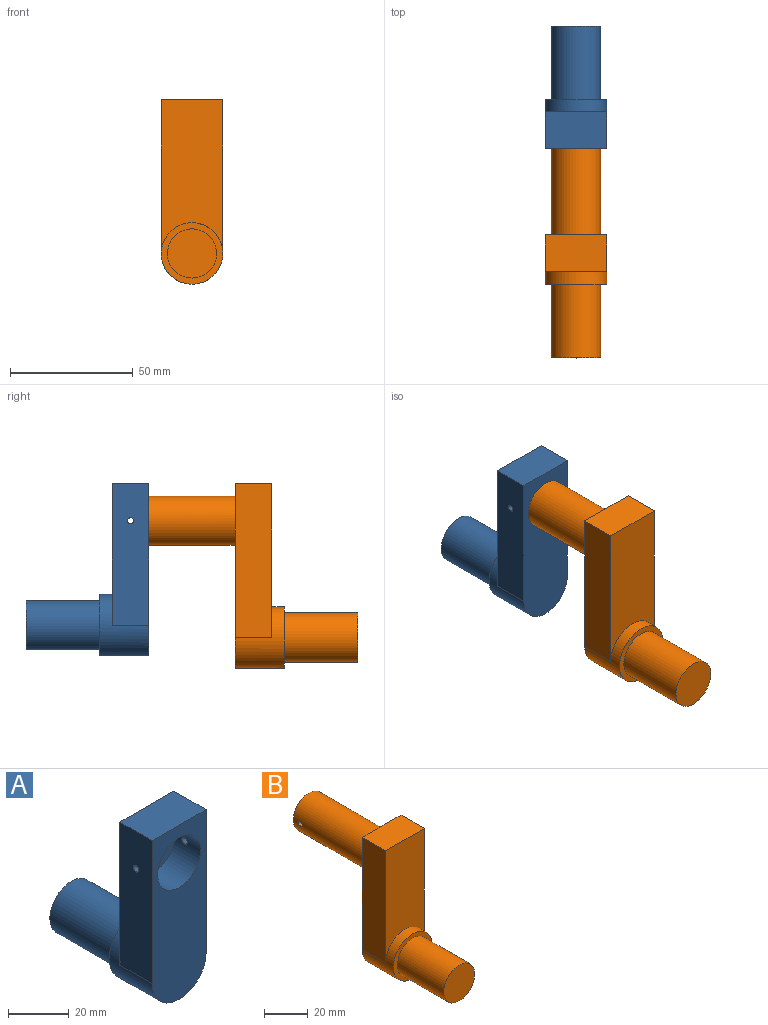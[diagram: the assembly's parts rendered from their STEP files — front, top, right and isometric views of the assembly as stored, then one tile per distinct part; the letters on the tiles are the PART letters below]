
ASSEMBLY  parts=2 mates=1
PART A: 13 faces, bbox 25x50x70 mm
  f0: plane 25x15mm, normal (0,0,1), area 375mm2, adj f1,f3,f4,f5
  f1: plane 57.5x15mm, normal (-1,0,0), area 857.6mm2, adj f0,f2,f4,f5,f12
  f2: cylinder r=12.5mm len=25mm, axis (0,1,0), area 981.7mm2, adj f1,f3,f4,f5,f6
  f3: plane 57.5x15mm, normal (1,0,0), area 857.6mm2, adj f0,f2,f4,f5,f11
  f4: plane 70x25mm, normal (0,-1,0), area 1368.8mm2, adj f0,f1,f2,f3,f9
  f5: plane 57.5x25mm, normal (0,1,0), area 1192.1mm2, adj f0,f1,f2,f3
  f6: plane 25x25mm, normal (0,1,0), area 176.7mm2, adj f2,f7
  f7: cylinder r=10mm len=30mm, axis (0,-1,0), area 1885mm2, adj f6,f8
  f8: plane 20x20mm, normal (0,1,0), area 314.2mm2, adj f7
  f9: cylinder r=10mm len=20mm, axis (0,-1,0), area 744.1mm2, adj f4,f10,f11,f12
  f10: plane 20x20mm, normal (0,-1,0), area 314.2mm2, adj f9
  f11: cylinder r=1.25mm len=2.58mm, axis (1,0,0), area 19.9mm2, adj f3,f9
  f12: cylinder r=1.25mm len=2.58mm, axis (1,0,0), area 19.9mm2, adj f1,f9
PART B: 12 faces, bbox 25x97x75 mm
  f0: cylinder r=10mm len=30mm, axis (0,1,0), area 1885mm2, adj f1,f3
  f1: plane 20x20mm, normal (0,-1,0), area 314.2mm2, adj f0
  f2: cylinder r=12.5mm len=25mm, axis (0,-1,0), area 981.7mm2, adj f3,f4,f5,f7,f8
  f3: plane 25x25mm, normal (0,-1,0), area 176.7mm2, adj f0,f2
  f4: plane 62.5x25mm, normal (0,-1,0), area 1317.1mm2, adj f2,f5,f6,f7
  f5: plane 62.5x15mm, normal (-1,0,0), area 937.5mm2, adj f2,f4,f6,f8
  f6: plane 25x15mm, normal (0,0,1), area 375mm2, adj f4,f5,f7,f8
  f7: plane 62.5x15mm, normal (1,0,0), area 937.5mm2, adj f2,f4,f6,f8
  f8: plane 75x25mm, normal (0,1,0), area 1493.8mm2, adj f2,f5,f6,f7,f9
  f9: cylinder r=10mm len=47mm, axis (0,-1,0), area 2943.3mm2, adj f8,f10,f11
  f10: plane 20x20mm, normal (0,1,0), area 314.2mm2, adj f9
  f11: cylinder r=1.25mm len=20mm, axis (-1,0,0), area 156.5mm2, adj f9
PLACE A t=(-31.2,46.31,23.39)mm
PLACE B t=(-32.24,-23.69,-4.87)mm
MATE fastened A.f9 <-> B.f9  axis (0,-1,0) through (-32.24,43.31,42.63)mm
